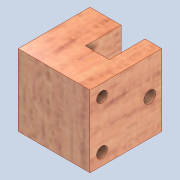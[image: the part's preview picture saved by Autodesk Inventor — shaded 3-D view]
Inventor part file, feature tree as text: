
AUTODESK INVENTOR PART (.ipt)
format: ipt  version: 2020 (Build 240168000, 168)  size: 163,840 bytes
history: native  units: mm
features: sketch x5, extrude x3, hole x2
ambient origin geometry x8: Origin, YZ Plane, XZ Plane, XY Plane, X Axis, Y Axis, Z Axis, Center Point
bodies: Solid1 (feature_tree)
feature tree (10):
  extrude  "Extrusion1"  Depth=30.0mm
  extrude  "Extrusion4"  Depth=10.0mm
  extrude  "Extrusion3"  Depth=15.0mm
  hole  "Hole1"  [1 undecoded]
  hole  "Hole2"  [1 undecoded]
  sketch  "Sketch1"  dims[d0=30.0mm d1=30.0mm]
  sketch  "Sketch4"  dims[d2=30.0mm d3=0.0mm d8=10.0mm]
  sketch  "Sketch5"  dims[d9=15.0mm d10=0.0mm d11=5.0mm]
  sketch  "Sketch6"  dims[d12=5.0mm d13=6.0mm d14=4.0mm d15=2.0mm d16=90.0deg d17=10.0mm d18=20.594885mm d19=4.5mm]
  sketch  "Sketch7"  dims[d20=5.0mm d21=5.0mm d22=5.0mm d23=0.0mm d24=0.0mm d25=7.0mm d26=4.134mm d27=10.0mm d28=4.0mm d29=2.0mm d30=90.0deg d31=10.0mm d32=20.594885mm]
note: 2 required parameter values undecoded (feature->parameter linkage not recoverable at this tier; creation-order binding heuristic only, values carry confidence <= 0.55)
